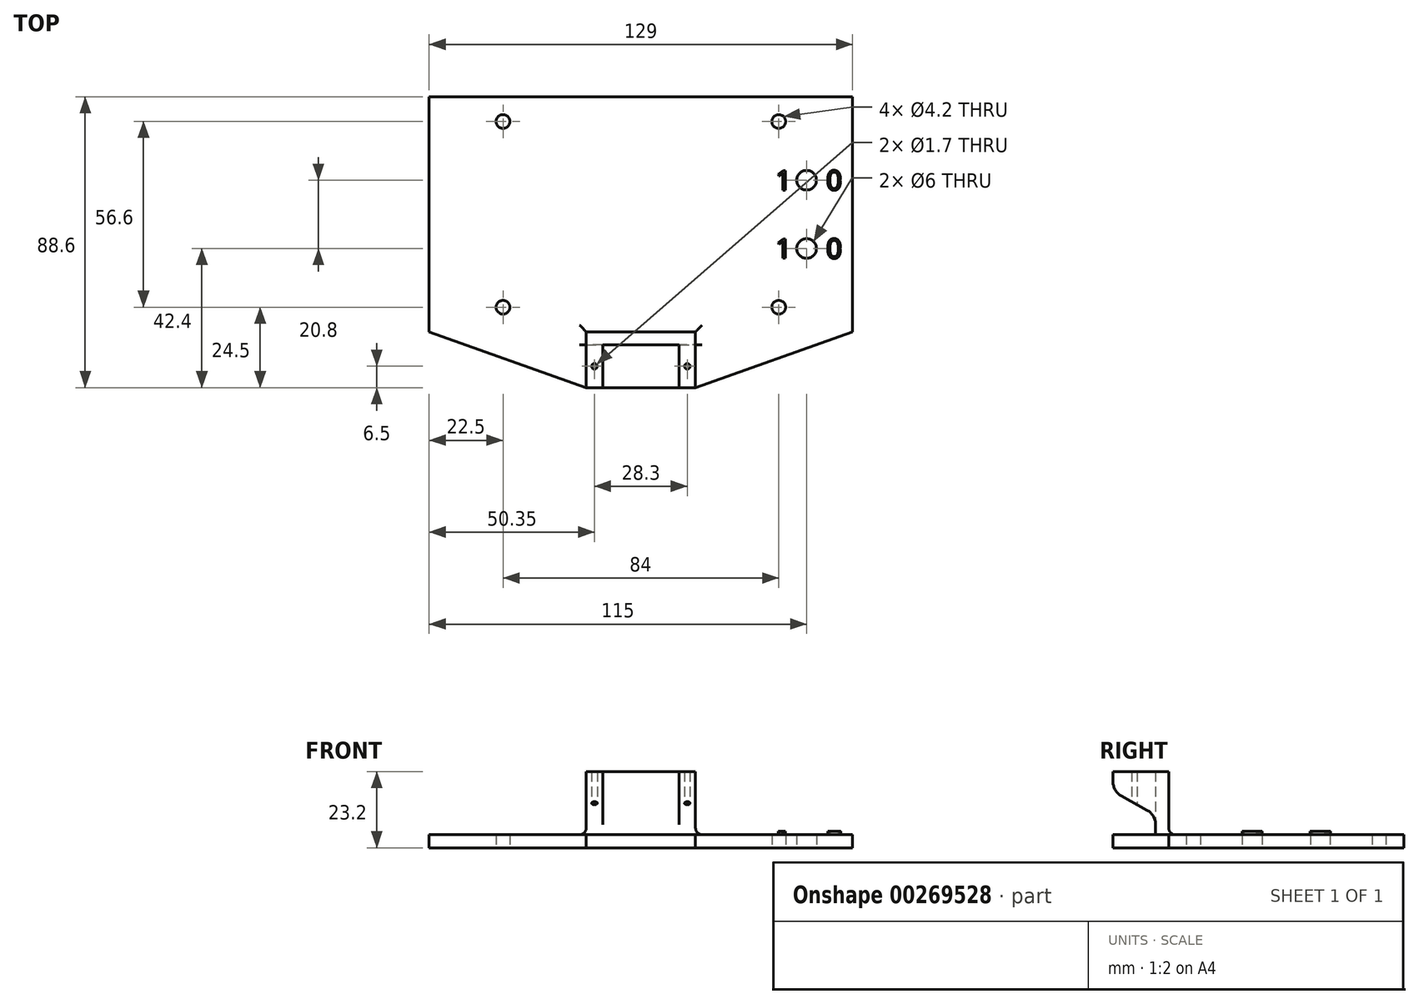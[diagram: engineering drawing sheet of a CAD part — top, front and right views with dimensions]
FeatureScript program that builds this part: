
annotation { "Feature Type Name" : "Feature", "Feature Type Description" : "" }
export const myFeature = defineFeature(function(context is Context, id is Id, definition is map)
    precondition{}
    {
        {
            var Q0;
            Q0=qCreatedBy(makeId("Top.planeOp"),FACE);
            var sketch = newSketch(context, id + "F0", { "sketchPlane" : qUnion([Q0])});
            skLineSegment(sketch, "E0.bottom", {"start": v(16.65, 8.5) * mm, "end": v(-16.65, 8.5) * mm});
            skLineSegment(sketch, "E0.top", {"start": v(16.65, -8.5) * mm, "end": v(-16.65, -8.5) * mm});
            skLineSegment(sketch, "E0.left", {"start": v(16.65, 8.5) * mm, "end": v(16.65, -8.5) * mm});
            skLineSegment(sketch, "E0.right", {"start": v(-16.65, 8.5) * mm, "end": v(-16.65, -8.5) * mm});
            skPoint(sketch, "E0.middle", {"position": v(0, 0) * mm});
            skLineSegment(sketch, "E1", {"start": v(11.65, -8.5) * mm, "end": v(11.65, 8.5) * mm});
            skLineSegment(sketch, "E2", {"start": v(-11.65, -8.5) * mm, "end": v(-11.65, 8.5) * mm});
            skLineSegment(sketch, "E3", {"start": v(-11.65, 4.5) * mm, "end": v(11.65, 4.5) * mm});
            skCircle(sketch, "E4", {"center": v(14.15, -2) * mm, "radius": 0.85 * mm});
            skCircle(sketch, "E5", {"center": v(-14.15, -2) * mm, "radius": 0.85 * mm});
            skCircle(sketch, "E6", {"center": v(-5.75, -2.2) * mm, "radius": 3.8 * mm});
            skCircle(sketch, "E7.MirrorC", {"center": v(5.75, -2.2) * mm, "radius": 3.8 * mm});
            skSolve(sketch);
        }
        {
            var Q0;
            Q0=qCreatedBy(makeId("Front.planeOp"),FACE);
            var sketch = newSketch(context, id + "F1", { "sketchPlane" : qUnion([Q0])});
            skLineSegment(sketch, "E8.bottom", {"start": v(-16.65, 0) * mm, "end": v(16.65, 0) * mm});
            skLineSegment(sketch, "E8.top", {"start": v(-16.65, 23.2) * mm, "end": v(16.65, 23.2) * mm});
            skLineSegment(sketch, "E8.left", {"start": v(-16.65, 0) * mm, "end": v(-16.65, 23.2) * mm});
            skLineSegment(sketch, "E8.right", {"start": v(16.65, 0) * mm, "end": v(16.65, 23.2) * mm});
            skLineSegment(sketch, "E9", {"start": v(-16.65, 4) * mm, "end": v(16.65, 4) * mm});
            skLineSegment(sketch, "E10", {"start": v(11.65, 0) * mm, "end": v(11.65, 23.2) * mm});
            skLineSegment(sketch, "E11", {"start": v(-11.65, 0) * mm, "end": v(-11.65, 23.2) * mm});
            skLineSegment(sketch, "E12", {"start": v(16.65, 10) * mm, "end": v(11.65, 10) * mm});
            skLineSegment(sketch, "E13", {"start": v(-11.65, 10) * mm, "end": v(-16.65, 10) * mm});
            skLineSegment(sketch, "E14", {"start": v(11.65, 17.2) * mm, "end": v(16.65, 17.2) * mm});
            skLineSegment(sketch, "E15", {"start": v(-11.65, 17.2) * mm, "end": v(-16.65, 17.2) * mm});
            skSolve(sketch);
        }
        {
            var Q0;
            Q0=qCreatedBy(makeId("Right.planeOp"),FACE);
            var sketch = newSketch(context, id + "F2", { "sketchPlane" : qUnion([Q0])});
            skLineSegment(sketch, "E16.bottom", {"start": v(-8.5, 0) * mm, "end": v(8.5, 0) * mm});
            skLineSegment(sketch, "E16.top", {"start": v(-8.5, 23.2) * mm, "end": v(8.5, 23.2) * mm});
            skLineSegment(sketch, "E16.left", {"start": v(-8.5, 20.15) * mm, "end": v(-8.5, 23.2) * mm});
            skLineSegment(sketch, "E16.right", {"start": v(8.5, 0) * mm, "end": v(8.5, 23.2) * mm});
            skLineSegment(sketch, "E17", {"start": v(4.5, 7.05) * mm, "end": v(4.5, 0) * mm});
            skLineSegment(sketch, "E18", {"start": v(4.5, 17.2) * mm, "end": v(-8.5, 17.2) * mm});
            skLineSegment(sketch, "E19", {"start": v(4.5, 4) * mm, "end": v(-8.5, 4) * mm});
            skLineSegment(sketch, "E20", {"start": v(-8.5, 10) * mm, "end": v(4.5, 10) * mm});
            skLineSegment(sketch, "E21", {"start": v(-5.92, 15.77) * mm, "end": v(1.92, 11.43) * mm});
            skArc(sketch, "E22.filletArc", {"start": v(-8.5, 20.15) * mm, "mid": v(-7.8, 17.6) * mm, "end": v(-5.92, 15.77) * mm});
            skArc(sketch, "E23.filletArc", {"start": v(4.5, 7.05) * mm, "mid": v(3.8, 9.6) * mm, "end": v(1.92, 11.43) * mm});
            skLineSegment(sketch, "E24", {"start": v(-8.5, 20.15) * mm, "end": v(-8.5, 0) * mm});
            skSolve(sketch);
        }
        {
            var Q0;
            {var subQ0=sQuery(id+"F1.wireOp",EDGE,"E13");Q0=makeQuery(id+"F1.imprint","IMPRINT",FACE,{"disambiguationData":[TD([[makeQuery(id+"F1.imprint","IMPRINT",EDGE,{"derivedFrom":subQ0}),-1.0]])]});}
            var Q1;
            {var subQ5=sQuery(id+"F1.wireOp",EDGE,"E15");Q1=makeQuery(id+"F1.imprint","IMPRINT",FACE,{"disambiguationData":[TD([[makeQuery(id+"F1.imprint","IMPRINT",EDGE,{"derivedFrom":subQ5}),-1.0]])]});}
            var Q2;
            {var subQ3=sQuery(id+"F1.wireOp",EDGE,"E13");Q2=makeQuery(id+"F1.imprint","IMPRINT",FACE,{"disambiguationData":[TD([[makeQuery(id+"F1.imprint","IMPRINT",EDGE,{"derivedFrom":subQ3}),1.0]])]});}
            var Q3;
            {var subQ0=sQuery(id+"F1.wireOp",EDGE,"E8.left");var subQ1=sQuery(id+"F1.wireOp",EDGE,"E8.bottom");var subQ2=makeQuery(id+"F1.imprint","INTERSECT",VERTEX,{"derivedFrom":[subQ1,subQ0]});Q3=makeQuery(id+"F1.imprint","IMPRINT",FACE,{"disambiguationData":[TD([[makeQuery(id+"F1.imprint","IMPRINT",EDGE,{"disambiguationData":[TD([[subQ2,-1.0]])],"derivedFrom":subQ1}),1.0]])]});}
            var Q4;
            {var subQ0=sQuery(id+"F1.wireOp",EDGE,"E10");var subQ1=sQuery(id+"F1.wireOp",EDGE,"E8.bottom");var subQ2=makeQuery(id+"F1.imprint","INTERSECT",VERTEX,{"derivedFrom":[subQ1,subQ0]});Q4=makeQuery(id+"F1.imprint","IMPRINT",FACE,{"disambiguationData":[TD([[makeQuery(id+"F1.imprint","IMPRINT",EDGE,{"disambiguationData":[TD([[subQ2,1.0]])],"derivedFrom":subQ1}),1.0]])]});}
            var Q5;
            {var subQ0=sQuery(id+"F1.wireOp",EDGE,"E8.right");var subQ1=sQuery(id+"F1.wireOp",EDGE,"E8.bottom");var subQ2=makeQuery(id+"F1.imprint","INTERSECT",VERTEX,{"derivedFrom":[subQ1,subQ0]});Q5=makeQuery(id+"F1.imprint","IMPRINT",FACE,{"disambiguationData":[TD([[makeQuery(id+"F1.imprint","IMPRINT",EDGE,{"disambiguationData":[TD([[subQ2,1.0]])],"derivedFrom":subQ1}),1.0]])]});}
            var Q6;
            {var subQ3=sQuery(id+"F1.wireOp",EDGE,"E12");Q6=makeQuery(id+"F1.imprint","IMPRINT",FACE,{"disambiguationData":[TD([[makeQuery(id+"F1.imprint","IMPRINT",EDGE,{"derivedFrom":subQ3}),1.0]])]});}
            var Q7;
            {var subQ0=sQuery(id+"F1.wireOp",EDGE,"E12");Q7=makeQuery(id+"F1.imprint","IMPRINT",FACE,{"disambiguationData":[TD([[makeQuery(id+"F1.imprint","IMPRINT",EDGE,{"derivedFrom":subQ0}),-1.0]])]});}
            var Q8;
            {var subQ5=sQuery(id+"F1.wireOp",EDGE,"E14");Q8=makeQuery(id+"F1.imprint","IMPRINT",FACE,{"disambiguationData":[TD([[makeQuery(id+"F1.imprint","IMPRINT",EDGE,{"derivedFrom":subQ5}),1.0]])]});}
            extrude(context, id + "F3", {"entities" : qUnion([Q0, Q1, Q2, Q3, Q4, Q5, Q6, Q7, Q8]), "endBound" : BoundingType.SYMMETRIC, "depth" : 17 * mm});
        }
        {
            var Q0;
            {var subQ5=sQuery(id+"F0.wireOp",EDGE,"E3");Q0=makeQuery(id+"F0.imprint","IMPRINT",FACE,{"disambiguationData":[TD([[makeQuery(id+"F0.imprint","IMPRINT",EDGE,{"derivedFrom":subQ5}),1.0]])]});}
            extrude(context, id + "F4", {"entities" : qUnion([Q0]), "operationType" : NewBodyOperationType.ADD, "depth" : 23.2 * mm});
        }
        {
            var Q0;
            {var subQ0=sQuery(id+"F2.wireOp",EDGE,"E21");Q0=makeQuery(id+"F2.imprint","IMPRINT",FACE,{"disambiguationData":[TD([[makeQuery(id+"F2.imprint","IMPRINT",EDGE,{"derivedFrom":subQ0}),-1.0]])]});}
            var Q1;
            {var subQ0=sQuery(id+"F2.wireOp",EDGE,"E24");var subQ1=sQuery(id+"F2.wireOp",EDGE,"E18");var subQ2=makeQuery(id+"F2.imprint","INTERSECT",VERTEX,{"derivedFrom":[subQ1,subQ0]});Q1=makeQuery(id+"F2.imprint","IMPRINT",FACE,{"disambiguationData":[TD([[makeQuery(id+"F2.imprint","IMPRINT",EDGE,{"disambiguationData":[TD([[subQ2,1.0]])],"derivedFrom":subQ1}),-1.0]])]});}
            var Q2;
            {var subQ5=sQuery(id+"F2.wireOp",EDGE,"E19");Q2=makeQuery(id+"F2.imprint","IMPRINT",FACE,{"disambiguationData":[TD([[makeQuery(id+"F2.imprint","IMPRINT",EDGE,{"derivedFrom":subQ5}),-1.0]])]});}
            extrude(context, id + "F5", {"entities" : qUnion([Q0, Q1, Q2]), "operationType" : NewBodyOperationType.REMOVE, "endBound" : BoundingType.SYMMETRIC, "oppositeDirection" : true, "depth" : 36.2 * mm});
        }
        {
            var Q0;
            Q0=makeQuery(id+"F0.imprint","IMPRINT",FACE,{"disambiguationData":[TD([[makeQuery(id+"F0.imprint","IMPRINT",EDGE,{"derivedFrom":sQuery(id+"F0.wireOp",EDGE,"E4")}),1.0]])]});
            var Q1;
            Q1=makeQuery(id+"F0.imprint","IMPRINT",FACE,{"disambiguationData":[TD([[makeQuery(id+"F0.imprint","IMPRINT",EDGE,{"derivedFrom":sQuery(id+"F0.wireOp",EDGE,"E5")}),1.0]])]});
            extrude(context, id + "F6", {"entities" : qUnion([Q0, Q1]), "operationType" : NewBodyOperationType.REMOVE, "depth" : 25 * mm, "hasSecondDirection" : true, "secondDirectionOppositeDirection" : false, "secondDirectionDepth" : 4.3 * mm});
        }
        {
            var Q0;
            Q0=qCreatedBy(makeId("Top.planeOp"),FACE);
            var sketch = newSketch(context, id + "F7", { "sketchPlane" : qUnion([Q0])});
            skLineSegment(sketch, "E25.bottom", {"start": v(-64.5, 80.1) * mm, "end": v(64.5, 80.1) * mm});
            skLineSegment(sketch, "E25.top", {"start": v(-64.5, 8.5) * mm, "end": v(64.5, 8.5) * mm});
            skLineSegment(sketch, "E25.left", {"start": v(-64.5, 80.1) * mm, "end": v(-64.5, 8.5) * mm});
            skLineSegment(sketch, "E25.right", {"start": v(64.5, 80.1) * mm, "end": v(64.5, 8.5) * mm});
            skPoint(sketch, "E26", {"position": v(0, 8.5) * mm});
            skLineSegment(sketch, "E27", {"start": v(0, 8.5) * mm, "end": v(0, 0) * mm});
            skLineSegment(sketch, "E28", {"start": v(64.5, 8.5) * mm, "end": v(16.65, -8.5) * mm});
            skLineSegment(sketch, "E29", {"start": v(16.65, -8.5) * mm, "end": v(-16.65, -8.5) * mm});
            skLineSegment(sketch, "E30", {"start": v(-16.65, -8.5) * mm, "end": v(-64.5, 8.5) * mm});
            skCircle(sketch, "E31", {"center": v(50.5, 33.9) * mm, "radius": 3 * mm});
            skCircle(sketch, "E32", {"center": v(50.5, 54.7) * mm, "radius": 3 * mm});
            skPoint(sketch, "E33", {"position": v(64.5, 44.3) * mm});
            skLineSegment(sketch, "E34", {"start": v(64.5, 44.3) * mm, "end": v(-64.5, 44.3) * mm});
            skText(sketch, "E35", { "text": "0", "fontName": "OpenSans-Regular.ttf"});
            skText(sketch, "E36", { "text": "1", "fontName": "OpenSans-Regular.ttf"});
            skPoint(sketch, "E37", {"position": v(44.5, 33.9) * mm});
            skPoint(sketch, "E38", {"position": v(56.5, 33.9) * mm});
            skLineSegment(sketch, "E39", {"start": v(44.5, 33.9) * mm, "end": v(50.5, 33.9) * mm});
            skLineSegment(sketch, "E40", {"start": v(56.5, 33.9) * mm, "end": v(50.5, 33.9) * mm});
            skText(sketch, "E41", { "text": "1\n", "fontName": "OpenSans-Regular.ttf"});
            skText(sketch, "E42", { "text": "0", "fontName": "OpenSans-Regular.ttf"});
            skPoint(sketch, "E43", {"position": v(44.5, 54.7) * mm});
            skPoint(sketch, "E44", {"position": v(56.5, 54.7) * mm});
            skLineSegment(sketch, "E45", {"start": v(50.5, 54.7) * mm, "end": v(44.5, 54.7) * mm});
            skLineSegment(sketch, "E46", {"start": v(56.5, 54.7) * mm, "end": v(50.5, 54.7) * mm});
            skCircle(sketch, "E47", {"center": v(42, 72.6) * mm, "radius": 2.1 * mm});
            skCircle(sketch, "E48.MirrorC", {"center": v(-42, 72.6) * mm, "radius": 2.1 * mm});
            skCircle(sketch, "E49.MirrorC", {"center": v(-42, 16) * mm, "radius": 2.1 * mm});
            skCircle(sketch, "E50.MirrorC", {"center": v(42, 16) * mm, "radius": 2.1 * mm});
            const initialGuessF7  = {"E35": [0.0565, 0.0309, 1, 0, 0.006], "E36": [0.04105, 0.0309, 1, 0, 0.006], "E41": [0.04105, 0.0517, 1, 0, 0.006], "E42": [0.0565, 0.0517, 1, 0, 0.006]};
            skSetInitialGuess(sketch, initialGuessF7);
            skSolve(sketch);
        }
        {
            var Q0;
            Q0=makeQuery(id+"F7.imprint","IMPRINT",FACE,{"disambiguationData":[TD([[makeQuery(id+"F7.imprint","IMPRINT",EDGE,{"derivedFrom":sQuery(id+"F7.wireOp",EDGE,"E35.sketch_text.stroke-0")}),-1.0]])]});
            var Q1;
            {var subQ3=sQuery(id+"F7.wireOp",EDGE,"E34");Q1=makeQuery(id+"F7.imprint","IMPRINT",FACE,{"disambiguationData":[TD([[makeQuery(id+"F7.imprint","IMPRINT",EDGE,{"derivedFrom":subQ3}),1.0]])]});}
            var Q2;
            Q2=makeQuery(id+"F7.imprint","IMPRINT",FACE,{"disambiguationData":[TD([[makeQuery(id+"F7.imprint","IMPRINT",EDGE,{"derivedFrom":sQuery(id+"F7.wireOp",EDGE,"E35.sketch_text.stroke-8")}),1.0]])]});
            var Q3;
            Q3=makeQuery(id+"F7.imprint","IMPRINT",FACE,{"disambiguationData":[TD([[makeQuery(id+"F7.imprint","IMPRINT",EDGE,{"derivedFrom":sQuery(id+"F7.wireOp",EDGE,"E36.sketch_text.stroke-0")}),-1.0]])]});
            var Q4;
            {var subQ1=sQuery(id+"F7.wireOp",EDGE,"E25.bottom");Q4=makeQuery(id+"F7.imprint","IMPRINT",FACE,{"disambiguationData":[TD([[makeQuery(id+"F7.imprint","IMPRINT",EDGE,{"derivedFrom":subQ1}),-1.0]])]});}
            var Q5;
            {var subQ0=sQuery(id+"F7.wireOp",EDGE,"E28");Q5=makeQuery(id+"F7.imprint","IMPRINT",FACE,{"disambiguationData":[TD([[makeQuery(id+"F7.imprint","IMPRINT",EDGE,{"derivedFrom":subQ0}),-1.0]])]});}
            var Q6;
            Q6=makeQuery(id+"F7.imprint","IMPRINT",FACE,{"disambiguationData":[TD([[makeQuery(id+"F7.imprint","IMPRINT",EDGE,{"derivedFrom":sQuery(id+"F7.wireOp",EDGE,"E42.sketch_text.stroke-0")}),-1.0]])]});
            var Q7;
            Q7=makeQuery(id+"F7.imprint","IMPRINT",FACE,{"disambiguationData":[TD([[makeQuery(id+"F7.imprint","IMPRINT",EDGE,{"derivedFrom":sQuery(id+"F7.wireOp",EDGE,"E42.sketch_text.stroke-8")}),1.0]])]});
            var Q8;
            Q8=makeQuery(id+"F7.imprint","IMPRINT",FACE,{"disambiguationData":[TD([[makeQuery(id+"F7.imprint","IMPRINT",EDGE,{"derivedFrom":sQuery(id+"F7.wireOp",EDGE,"E41.sketch_text.stroke-0")}),-1.0]])]});
            extrude(context, id + "F8", {"entities" : qUnion([Q0, Q1, Q2, Q3, Q4, Q5, Q6, Q7, Q8]), "operationType" : NewBodyOperationType.ADD, "depth" : 4 * mm, "offsetDistance" : 25 * mm});
        }
        {
            var Q0;
            Q0=makeQuery(id+"F7.imprint","IMPRINT",FACE,{"disambiguationData":[TD([[makeQuery(id+"F7.imprint","IMPRINT",EDGE,{"derivedFrom":sQuery(id+"F7.wireOp",EDGE,"E36.sketch_text.stroke-0")}),-1.0]])]});
            var Q1;
            Q1=makeQuery(id+"F7.imprint","IMPRINT",FACE,{"disambiguationData":[TD([[makeQuery(id+"F7.imprint","IMPRINT",EDGE,{"derivedFrom":sQuery(id+"F7.wireOp",EDGE,"E35.sketch_text.stroke-0")}),-1.0]])]});
            var Q2;
            Q2=makeQuery(id+"F7.imprint","IMPRINT",FACE,{"disambiguationData":[TD([[makeQuery(id+"F7.imprint","IMPRINT",EDGE,{"derivedFrom":sQuery(id+"F7.wireOp",EDGE,"E41.sketch_text.stroke-0")}),-1.0]])]});
            var Q3;
            Q3=makeQuery(id+"F7.imprint","IMPRINT",FACE,{"disambiguationData":[TD([[makeQuery(id+"F7.imprint","IMPRINT",EDGE,{"derivedFrom":sQuery(id+"F7.wireOp",EDGE,"E42.sketch_text.stroke-0")}),-1.0]])]});
            extrude(context, id + "F9", {"entities" : qUnion([Q0, Q1, Q2, Q3]), "operationType" : NewBodyOperationType.ADD, "depth" : 5 * mm, "offsetDistance" : 25 * mm});
        }
        {
            var Q0;
            Q0=makeQuery(id+"F8.boolean.opBoolean","INTERSECT",EDGE,{"derivedFrom":[makeQuery(id+"F4.boolean.opBoolean","MERGE",FACE,{"derivedFrom":[makeQuery(id+"F3.opExtrude","CAP_FACE",FACE,{"disambiguationData":[OSD([sQuery(id+"F1.wireOp",EDGE,"E8.bottom"),sQuery(id+"F1.wireOp",EDGE,"E8.top"),sQuery(id+"F1.wireOp",EDGE,"E8.left"),sQuery(id+"F1.wireOp",EDGE,"E8.right"),sQuery(id+"F1.wireOp",EDGE,"E9"),sQuery(id+"F1.wireOp",EDGE,"E10"),sQuery(id+"F1.wireOp",EDGE,"E11")])],"isStart":true}),makeQuery(id+"F4.opExtrude","SWEPT_FACE",FACE,{"disambiguationData":[OSD([sQuery(id+"F0.wireOp",EDGE,"E0.bottom")])]})]}),makeQuery(id+"F8.opExtrude","CAP_FACE",FACE,{"disambiguationData":[OSD([sQuery(id+"F7.wireOp",EDGE,"E25.bottom"),sQuery(id+"F7.wireOp",EDGE,"E25.left"),sQuery(id+"F7.wireOp",EDGE,"E25.right"),sQuery(id+"F7.wireOp",EDGE,"E28"),sQuery(id+"F7.wireOp",EDGE,"E29"),sQuery(id+"F7.wireOp",EDGE,"E30"),sQuery(id+"F7.wireOp",EDGE,"E31"),sQuery(id+"F7.wireOp",EDGE,"E32"),sQuery(id+"F7.wireOp",EDGE,"E47"),sQuery(id+"F7.wireOp",EDGE,"E48.MirrorC"),sQuery(id+"F7.wireOp",EDGE,"E49.MirrorC"),sQuery(id+"F7.wireOp",EDGE,"E50.MirrorC")])],"isStart":false})]});
            var Q1;
            Q1=makeQuery(id+"F8.boolean.opBoolean","INTERSECT",EDGE,{"derivedFrom":[makeQuery(id+"F3.opExtrude","SWEPT_FACE",FACE,{"disambiguationData":[OSD([sQuery(id+"F1.wireOp",EDGE,"E8.right")])]}),makeQuery(id+"F8.opExtrude","CAP_FACE",FACE,{"disambiguationData":[OSD([sQuery(id+"F7.wireOp",EDGE,"E25.bottom"),sQuery(id+"F7.wireOp",EDGE,"E25.left"),sQuery(id+"F7.wireOp",EDGE,"E25.right"),sQuery(id+"F7.wireOp",EDGE,"E28"),sQuery(id+"F7.wireOp",EDGE,"E29"),sQuery(id+"F7.wireOp",EDGE,"E30"),sQuery(id+"F7.wireOp",EDGE,"E31"),sQuery(id+"F7.wireOp",EDGE,"E32"),sQuery(id+"F7.wireOp",EDGE,"E47"),sQuery(id+"F7.wireOp",EDGE,"E48.MirrorC"),sQuery(id+"F7.wireOp",EDGE,"E49.MirrorC"),sQuery(id+"F7.wireOp",EDGE,"E50.MirrorC")])],"isStart":false})]});
            var Q2;
            Q2=makeQuery(id+"F8.boolean.opBoolean","INTERSECT",EDGE,{"derivedFrom":[makeQuery(id+"F3.opExtrude","SWEPT_FACE",FACE,{"disambiguationData":[OSD([sQuery(id+"F1.wireOp",EDGE,"E8.left")])]}),makeQuery(id+"F8.opExtrude","CAP_FACE",FACE,{"disambiguationData":[OSD([sQuery(id+"F7.wireOp",EDGE,"E25.bottom"),sQuery(id+"F7.wireOp",EDGE,"E25.left"),sQuery(id+"F7.wireOp",EDGE,"E25.right"),sQuery(id+"F7.wireOp",EDGE,"E28"),sQuery(id+"F7.wireOp",EDGE,"E29"),sQuery(id+"F7.wireOp",EDGE,"E30"),sQuery(id+"F7.wireOp",EDGE,"E31"),sQuery(id+"F7.wireOp",EDGE,"E32"),sQuery(id+"F7.wireOp",EDGE,"E47"),sQuery(id+"F7.wireOp",EDGE,"E48.MirrorC"),sQuery(id+"F7.wireOp",EDGE,"E49.MirrorC"),sQuery(id+"F7.wireOp",EDGE,"E50.MirrorC")])],"isStart":false})]});
            fillet(context, id + "F10", {"entities" : qUnion([Q0, Q1, Q2]), "radius" : 2 * mm, "tangentPropagation" : true, "allowEdgeOverflow" : false});
        }
    });
